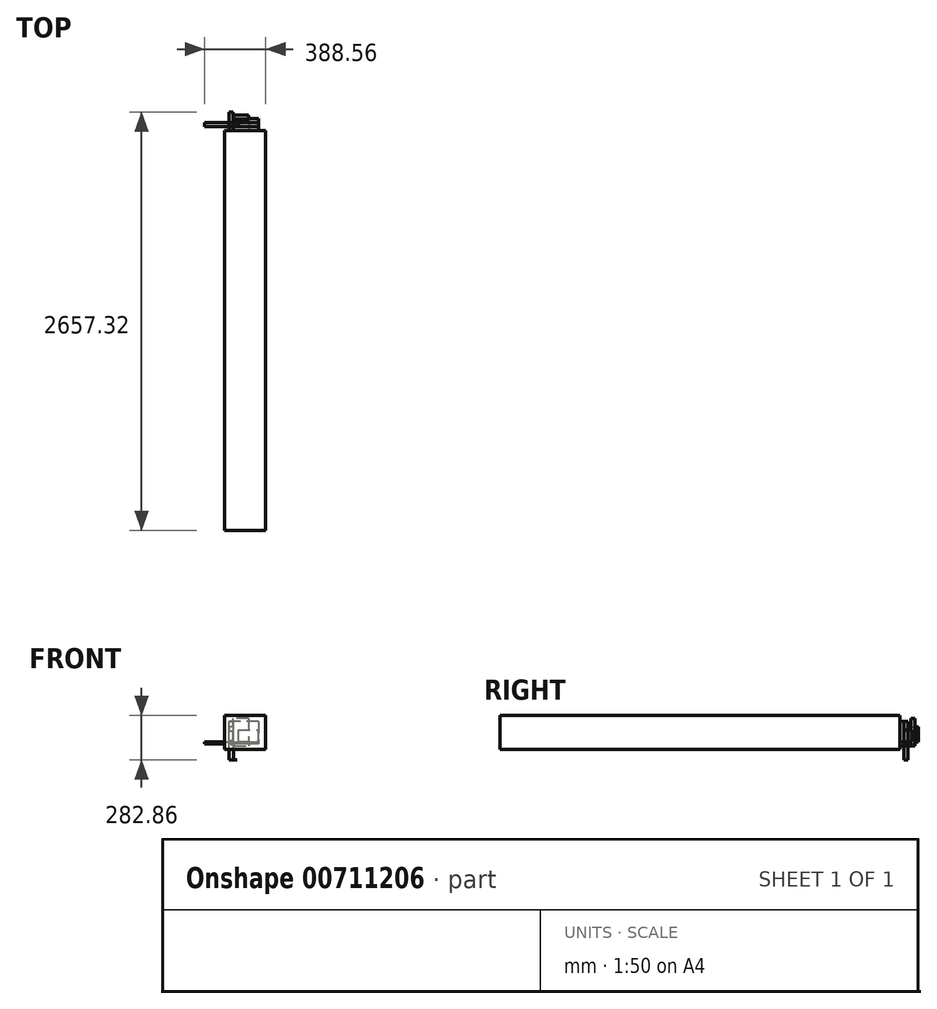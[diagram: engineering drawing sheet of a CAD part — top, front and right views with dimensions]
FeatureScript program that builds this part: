
annotation { "Feature Type Name" : "Feature", "Feature Type Description" : "" }
export const myFeature = defineFeature(function(context is Context, id is Id, definition is map)
    precondition{}
    {
        {
            var Q0;
            Q0=qCreatedBy(makeId("Front.planeOp"),FACE);
            var sketch = newSketch(context, id + "F0", { "sketchPlane" : qUnion([Q0])});
            skLineSegment(sketch, "E0.bottom", {"start": v(0, 0) * mm, "end": v(78.63, 0) * mm});
            skLineSegment(sketch, "E0.top", {"start": v(0, -50.24) * mm, "end": v(78.63, -50.24) * mm});
            skLineSegment(sketch, "E0.left", {"start": v(0, 0) * mm, "end": v(0, -50.24) * mm});
            skLineSegment(sketch, "E0.right", {"start": v(78.63, 0) * mm, "end": v(78.63, -50.24) * mm});
            skLineSegment(sketch, "E1.bottom", {"start": v(78.63, 0) * mm, "end": v(-83, 0) * mm});
            skLineSegment(sketch, "E1.top", {"start": v(78.63, 52.99) * mm, "end": v(-83, 52.99) * mm});
            skLineSegment(sketch, "E1.left", {"start": v(78.63, 0) * mm, "end": v(78.63, 52.99) * mm});
            skLineSegment(sketch, "E1.right", {"start": v(-83, 0) * mm, "end": v(-83, 52.99) * mm});
            skLineSegment(sketch, "E2.bottom", {"start": v(-83, 0) * mm, "end": v(0, 0) * mm});
            skLineSegment(sketch, "E2.top", {"start": v(-83, -50.24) * mm, "end": v(0, -50.24) * mm});
            skLineSegment(sketch, "E2.left", {"start": v(-83, 0) * mm, "end": v(-83, -50.24) * mm});
            skSolve(sketch);
        }
        {
            var Q0;
            Q0 = qSketchRegion(id + "F0", true);
            extrude(context, id + "F1", {"entities" : qUnion([Q0]), "depth" : 25.4 * mm, "offsetDistance" : 25.4 * mm});
        }
        {
            var Q0;
            Q0=makeQuery(id+"F1.opExtrude","SWEPT_FACE",FACE,{"disambiguationData":[OSD([sQuery(id+"F0.wireOp",EDGE,"E0.top"),sQuery(id+"F0.wireOp",EDGE,"E2.top")])]});
            var sketch = newSketch(context, id + "F2", { "sketchPlane" : qUnion([Q0])});
            skLineSegment(sketch, "E3.bottom", {"start": v(-56.4, 25.75) * mm, "end": v(78.63, 25.75) * mm});
            skLineSegment(sketch, "E3.top", {"start": v(-56.4, 0) * mm, "end": v(78.63, 0) * mm});
            skLineSegment(sketch, "E3.left", {"start": v(-56.4, 25.75) * mm, "end": v(-56.4, 0) * mm});
            skLineSegment(sketch, "E3.right", {"start": v(78.63, 25.75) * mm, "end": v(78.63, 0) * mm});
            skLineSegment(sketch, "E4.bottom", {"start": v(-56.4, 0) * mm, "end": v(-83, 0) * mm});
            skLineSegment(sketch, "E4.top", {"start": v(-56.4, 25.4) * mm, "end": v(-83, 25.4) * mm});
            skLineSegment(sketch, "E4.left", {"start": v(-56.4, 0) * mm, "end": v(-56.4, 25.4) * mm});
            skLineSegment(sketch, "E4.right", {"start": v(-83, 0) * mm, "end": v(-83, 25.4) * mm});
            skLineSegment(sketch, "E5.bottom", {"start": v(-56.4, 25.4) * mm, "end": v(77.16, 25.4) * mm});
            skLineSegment(sketch, "E5.top", {"start": v(-56.4, 25.4) * mm, "end": v(77.16, 25.4) * mm});
            skLineSegment(sketch, "E5.left", {"start": v(-56.4, 25.4) * mm, "end": v(-56.4, 25.4) * mm});
            skLineSegment(sketch, "E5.right", {"start": v(77.16, 25.4) * mm, "end": v(77.16, 25.4) * mm});
            skLineSegment(sketch, "E6.bottom", {"start": v(78.63, 0) * mm, "end": v(77.16, 0) * mm});
            skLineSegment(sketch, "E6.top", {"start": v(78.63, 25.4) * mm, "end": v(77.16, 25.4) * mm});
            skLineSegment(sketch, "E6.left", {"start": v(78.63, 0) * mm, "end": v(78.63, 25.4) * mm});
            skLineSegment(sketch, "E6.right", {"start": v(77.16, 0) * mm, "end": v(77.16, 25.4) * mm});
            skLineSegment(sketch, "E7.bottom", {"start": v(-56.4, 12.7) * mm, "end": v(-83, 12.7) * mm});
            skLineSegment(sketch, "E7.left", {"start": v(-56.4, 12.7) * mm, "end": v(-56.4, 0) * mm});
            skLineSegment(sketch, "E7.right", {"start": v(-83, 12.7) * mm, "end": v(-83, 0) * mm});
            skSolve(sketch);
        }
        {
            var Q0;
            Q0 = qSketchRegion(id + "F2", true);
            extrude(context, id + "F3", {"entities" : qUnion([Q0]), "operationType" : NewBodyOperationType.ADD, "depth" : 25.4 * mm, "offsetDistance" : 25.4 * mm});
        }
        {
            var Q0;
            Q0=makeQuery(id+"F3.boolean.opBoolean","MERGE",FACE,{"derivedFrom":[makeQuery(id+"F1.opExtrude","CAP_FACE",FACE,{"disambiguationData":[OSD([sQuery(id+"F0.wireOp",EDGE,"E0.top"),sQuery(id+"F0.wireOp",EDGE,"E0.right"),sQuery(id+"F0.wireOp",EDGE,"E1.top"),sQuery(id+"F0.wireOp",EDGE,"E1.left"),sQuery(id+"F0.wireOp",EDGE,"E1.right"),sQuery(id+"F0.wireOp",EDGE,"E2.top"),sQuery(id+"F0.wireOp",EDGE,"E2.left")])],"isStart":false}),makeQuery(id+"F3.opExtrude","SWEPT_FACE",FACE,{"disambiguationData":[OSD([sQuery(id+"F2.wireOp",EDGE,"E4.top")])]})]});
            var sketch = newSketch(context, id + "F4", { "sketchPlane" : qUnion([Q0])});
            skLineSegment(sketch, "E8.bottom", {"start": v(124.19, 91.37) * mm, "end": v(-137.15, 91.37) * mm});
            skLineSegment(sketch, "E8.top", {"start": v(124.19, -123.53) * mm, "end": v(-137.15, -123.53) * mm});
            skLineSegment(sketch, "E8.left", {"start": v(124.19, 91.37) * mm, "end": v(124.19, -123.53) * mm});
            skLineSegment(sketch, "E8.right", {"start": v(-137.15, 91.37) * mm, "end": v(-137.15, -123.53) * mm});
            skSolve(sketch);
        }
        {
            var Q0;
            Q0 = qSketchRegion(id + "F4", true);
            extrude(context, id + "F5", {"entities" : qUnion([Q0]), "operationType" : NewBodyOperationType.ADD, "depth" : 2540 * mm, "offsetDistance" : 25.4 * mm});
        }
        {
            var Q0;
            Q0=makeQuery(id+"F3.boolean.opBoolean","MERGE",FACE,{"derivedFrom":[makeQuery(id+"F1.opExtrude","SWEPT_FACE",FACE,{"disambiguationData":[OSD([sQuery(id+"F0.wireOp",EDGE,"E1.right"),sQuery(id+"F0.wireOp",EDGE,"E2.left")])]}),makeQuery(id+"F3.opExtrude","SWEPT_FACE",FACE,{"disambiguationData":[OSD([sQuery(id+"F2.wireOp",EDGE,"E4.right"),sQuery(id+"F2.wireOp",EDGE,"E7.right")])]})]});
            var sketch = newSketch(context, id + "F6", { "sketchPlane" : qUnion([Q0])});
            skLineSegment(sketch, "E9.bottom", {"start": v(0, -75.64) * mm, "end": v(-91.92, -75.64) * mm});
            skLineSegment(sketch, "E9.top", {"start": v(0, -7.44) * mm, "end": v(-91.92, -7.44) * mm});
            skLineSegment(sketch, "E9.left", {"start": v(0, -75.64) * mm, "end": v(0, -7.44) * mm});
            skLineSegment(sketch, "E9.right", {"start": v(-91.92, -75.64) * mm, "end": v(-91.92, -7.44) * mm});
            skSolve(sketch);
        }
        {
            var Q0;
            Q0 = qSketchRegion(id + "F6", true);
            extrude(context, id + "F7", {"entities" : qUnion([Q0]), "depth" : 25.4 * mm, "offsetDistance" : 25.4 * mm});
        }
        {
            var Q0;
            Q0=makeQuery(id+"F3.boolean.opBoolean","MERGE",FACE,{"derivedFrom":[makeQuery(id+"F1.opExtrude","SWEPT_FACE",FACE,{"disambiguationData":[OSD([sQuery(id+"F0.wireOp",EDGE,"E1.right"),sQuery(id+"F0.wireOp",EDGE,"E2.left")])]}),makeQuery(id+"F3.opExtrude","SWEPT_FACE",FACE,{"disambiguationData":[OSD([sQuery(id+"F2.wireOp",EDGE,"E4.right"),sQuery(id+"F2.wireOp",EDGE,"E7.right")])]})]});
            var sketch = newSketch(context, id + "F8", { "sketchPlane" : qUnion([Q0])});
            skLineSegment(sketch, "E10.bottom", {"start": v(0, -58.88) * mm, "end": v(18.18, -58.88) * mm});
            skLineSegment(sketch, "E10.top", {"start": v(0, -75.64) * mm, "end": v(18.18, -75.64) * mm});
            skLineSegment(sketch, "E10.left", {"start": v(0, -58.88) * mm, "end": v(0, -75.64) * mm});
            skLineSegment(sketch, "E10.right", {"start": v(18.18, -58.88) * mm, "end": v(18.18, -75.64) * mm});
            skLineSegment(sketch, "E11.bottom", {"start": v(18.18, -75.64) * mm, "end": v(25.4, -75.64) * mm});
            skLineSegment(sketch, "E11.top", {"start": v(18.18, 52.99) * mm, "end": v(25.4, 52.99) * mm});
            skLineSegment(sketch, "E11.left", {"start": v(18.18, -75.64) * mm, "end": v(18.18, 52.99) * mm});
            skLineSegment(sketch, "E11.right", {"start": v(25.4, -75.64) * mm, "end": v(25.4, 52.99) * mm});
            skLineSegment(sketch, "E12.bottom", {"start": v(18.18, 52.99) * mm, "end": v(0, 52.99) * mm});
            skLineSegment(sketch, "E12.top", {"start": v(18.18, -75.64) * mm, "end": v(0, -75.64) * mm});
            skLineSegment(sketch, "E12.left", {"start": v(18.18, 52.99) * mm, "end": v(18.18, -75.64) * mm});
            skLineSegment(sketch, "E12.right", {"start": v(0, 52.99) * mm, "end": v(0, -75.64) * mm});
            skLineSegment(sketch, "E13.bottom", {"start": v(25.4, -75.64) * mm, "end": v(25.4, -75.64) * mm});
            skLineSegment(sketch, "E13.top", {"start": v(25.4, 52.99) * mm, "end": v(25.4, 52.99) * mm});
            skSolve(sketch);
        }
        {
            var Q0;
            Q0 = qSketchRegion(id + "F8", true);
            extrude(context, id + "F9", {"entities" : qUnion([Q0]), "depth" : 25.4 * mm, "offsetDistance" : 25.4 * mm});
        }
        {
            var Q0;
            Q0=makeQuery(id+"F9.opExtrude","SWEPT_FACE",FACE,{"disambiguationData":[OSD([sQuery(id+"F8.wireOp",EDGE,"E12.right")])]});
            var sketch = newSketch(context, id + "F10", { "sketchPlane" : qUnion([Q0])});
            skLineSegment(sketch, "E14.bottom", {"start": v(58.99, -191.49) * mm, "end": v(78.82, -191.49) * mm});
            skLineSegment(sketch, "E14.top", {"start": v(58.99, -190.19) * mm, "end": v(78.82, -190.19) * mm});
            skLineSegment(sketch, "E14.left", {"start": v(58.99, -191.49) * mm, "end": v(58.99, -190.19) * mm});
            skLineSegment(sketch, "E14.right", {"start": v(78.82, -191.49) * mm, "end": v(78.82, -190.19) * mm});
            skLineSegment(sketch, "E15.bottom", {"start": v(78.82, -190.19) * mm, "end": v(108.4, -190.19) * mm});
            skLineSegment(sketch, "E15.top", {"start": v(78.82, 52.99) * mm, "end": v(108.4, 52.99) * mm});
            skLineSegment(sketch, "E15.left", {"start": v(78.82, -190.19) * mm, "end": v(78.82, 52.99) * mm});
            skLineSegment(sketch, "E15.right", {"start": v(108.4, -190.19) * mm, "end": v(108.4, 52.99) * mm});
            skSolve(sketch);
        }
        {
            var Q0;
            Q0 = qSketchRegion(id + "F10", true);
            extrude(context, id + "F11", {"entities" : qUnion([Q0]), "depth" : 25.4 * mm, "offsetDistance" : 25.4 * mm});
        }
        {
            var Q0;
            Q0=makeQuery(id+"F7.opExtrude","SWEPT_FACE",FACE,{"disambiguationData":[OSD([sQuery(id+"F6.wireOp",EDGE,"E9.top")])]});
            var sketch = newSketch(context, id + "F12", { "sketchPlane" : qUnion([Q0])});
            skLineSegment(sketch, "E16.bottom", {"start": v(-108.4, 91.92) * mm, "end": v(-83, 91.92) * mm});
            skLineSegment(sketch, "E16.top", {"start": v(-108.4, 91.92) * mm, "end": v(-83, 91.92) * mm});
            skLineSegment(sketch, "E16.left", {"start": v(-108.4, 91.92) * mm, "end": v(-108.4, 91.92) * mm});
            skLineSegment(sketch, "E16.right", {"start": v(-83, 91.92) * mm, "end": v(-83, 91.92) * mm});
            skLineSegment(sketch, "E17.bottom", {"start": v(-83, 91.92) * mm, "end": v(-108.4, 91.92) * mm});
            skLineSegment(sketch, "E17.top", {"start": v(-83, 20.87) * mm, "end": v(-108.4, 20.87) * mm});
            skLineSegment(sketch, "E17.left", {"start": v(-83, 91.92) * mm, "end": v(-83, 20.87) * mm});
            skLineSegment(sketch, "E17.right", {"start": v(-108.4, 91.92) * mm, "end": v(-108.4, 20.87) * mm});
            skSolve(sketch);
        }
        {
            var Q0;
            Q0 = qSketchRegion(id + "F12", true);
            extrude(context, id + "F13", {"entities" : qUnion([Q0]), "depth" : 25.4 * mm, "offsetDistance" : 25.4 * mm});
        }
        {
            var Q0;
            Q0=makeQuery(id+"F3.boolean.opBoolean","MERGE",FACE,{"derivedFrom":[makeQuery(id+"F1.opExtrude","CAP_FACE",FACE,{"disambiguationData":[OSD([sQuery(id+"F0.wireOp",EDGE,"E0.top"),sQuery(id+"F0.wireOp",EDGE,"E0.right"),sQuery(id+"F0.wireOp",EDGE,"E1.top"),sQuery(id+"F0.wireOp",EDGE,"E1.left"),sQuery(id+"F0.wireOp",EDGE,"E1.right"),sQuery(id+"F0.wireOp",EDGE,"E2.top"),sQuery(id+"F0.wireOp",EDGE,"E2.left")])],"isStart":true}),makeQuery(id+"F3.opExtrude","SWEPT_FACE",FACE,{"disambiguationData":[OSD([sQuery(id+"F2.wireOp",EDGE,"E3.top"),sQuery(id+"F2.wireOp",EDGE,"E6.bottom"),sQuery(id+"F2.wireOp",EDGE,"E4.bottom")])]})]});
            var sketch = newSketch(context, id + "F14", { "sketchPlane" : qUnion([Q0])});
            skLineSegment(sketch, "E18.bottom", {"start": v(78.47, -80.98) * mm, "end": v(101.83, -80.98) * mm});
            skLineSegment(sketch, "E18.top", {"start": v(78.47, -69.53) * mm, "end": v(101.83, -69.53) * mm});
            skLineSegment(sketch, "E18.left", {"start": v(78.47, -80.98) * mm, "end": v(78.47, -69.53) * mm});
            skLineSegment(sketch, "E18.right", {"start": v(101.83, -80.98) * mm, "end": v(101.83, -69.53) * mm});
            skLineSegment(sketch, "E19.bottom", {"start": v(78.47, -80.98) * mm, "end": v(100.27, -80.98) * mm});
            skLineSegment(sketch, "E19.top", {"start": v(78.47, -80.98) * mm, "end": v(100.27, -80.98) * mm});
            skLineSegment(sketch, "E19.left", {"start": v(78.47, -80.98) * mm, "end": v(78.47, -80.98) * mm});
            skLineSegment(sketch, "E19.right", {"start": v(100.27, -80.98) * mm, "end": v(100.27, -80.98) * mm});
            skLineSegment(sketch, "E20.bottom", {"start": v(100.27, -80.98) * mm, "end": v(78.47, -80.98) * mm});
            skLineSegment(sketch, "E20.top", {"start": v(100.27, -91.98) * mm, "end": v(78.47, -91.98) * mm});
            skLineSegment(sketch, "E20.left", {"start": v(100.27, -80.98) * mm, "end": v(100.27, -91.98) * mm});
            skLineSegment(sketch, "E20.right", {"start": v(78.47, -80.98) * mm, "end": v(78.47, -91.98) * mm});
            skSolve(sketch);
        }
        {
            var Q0;
            Q0 = qSketchRegion(id + "F14", true);
            extrude(context, id + "F15", {"entities" : qUnion([Q0]), "depth" : 25.4 * mm, "offsetDistance" : 25.4 * mm});
        }
        {
            var Q0;
            Q0=makeQuery(id+"F3.opExtrude","CAP_FACE",FACE,{"disambiguationData":[OSD([sQuery(id+"F2.wireOp",EDGE,"E3.bottom"),sQuery(id+"F2.wireOp",EDGE,"E3.top"),sQuery(id+"F2.wireOp",EDGE,"E3.left"),sQuery(id+"F2.wireOp",EDGE,"E3.right"),sQuery(id+"F2.wireOp",EDGE,"E4.top"),sQuery(id+"F2.wireOp",EDGE,"E4.right"),sQuery(id+"F2.wireOp",EDGE,"E6.bottom"),sQuery(id+"F2.wireOp",EDGE,"E6.left"),sQuery(id+"F2.wireOp",EDGE,"E4.bottom"),sQuery(id+"F2.wireOp",EDGE,"E7.right")])],"isStart":false});
            var sketch = newSketch(context, id + "F16", { "sketchPlane" : qUnion([Q0])});
            skLineSegment(sketch, "E21.bottom", {"start": v(-74.07, 25.4) * mm, "end": v(21.2, 25.4) * mm});
            skLineSegment(sketch, "E21.top", {"start": v(-74.07, -47.2) * mm, "end": v(21.2, -47.2) * mm});
            skLineSegment(sketch, "E21.left", {"start": v(-74.07, 25.4) * mm, "end": v(-74.07, -47.2) * mm});
            skLineSegment(sketch, "E21.right", {"start": v(21.2, 25.4) * mm, "end": v(21.2, -47.2) * mm});
            skSolve(sketch);
        }
        {
            var Q0;
            Q0 = qSketchRegion(id + "F16", true);
            extrude(context, id + "F17", {"entities" : qUnion([Q0]), "operationType" : NewBodyOperationType.ADD, "depth" : 25.4 * mm, "offsetDistance" : 25.4 * mm});
        }
        {
            var Q0;
            Q0=makeQuery(id+"F17.opExtrude","SWEPT_FACE",FACE,{"disambiguationData":[OSD([sQuery(id+"F16.wireOp",EDGE,"E21.top")])]});
            var sketch = newSketch(context, id + "F18", { "sketchPlane" : qUnion([Q0])});
            skLineSegment(sketch, "E22.bottom", {"start": v(74.07, -88.34) * mm, "end": v(-14.84, -88.34) * mm});
            skLineSegment(sketch, "E22.top", {"start": v(74.07, -101.04) * mm, "end": v(-14.84, -101.04) * mm});
            skLineSegment(sketch, "E22.left", {"start": v(74.07, -88.34) * mm, "end": v(74.07, -101.04) * mm});
            skLineSegment(sketch, "E22.right", {"start": v(-14.84, -88.34) * mm, "end": v(-14.84, -101.04) * mm});
            skLineSegment(sketch, "E23.bottom", {"start": v(-14.84, -88.34) * mm, "end": v(83.82, -88.34) * mm});
            skLineSegment(sketch, "E23.top", {"start": v(-14.84, 73.44) * mm, "end": v(83.82, 73.44) * mm});
            skLineSegment(sketch, "E23.left", {"start": v(-14.84, -88.34) * mm, "end": v(-14.84, 73.44) * mm});
            skLineSegment(sketch, "E23.right", {"start": v(83.82, -88.34) * mm, "end": v(83.82, 73.44) * mm});
            skSolve(sketch);
        }
        {
            var Q0;
            Q0 = qSketchRegion(id + "F18", true);
            extrude(context, id + "F19", {"entities" : qUnion([Q0]), "depth" : 25.4 * mm, "offsetDistance" : 25.4 * mm});
        }
        {
            var Q0;
            Q0=makeQuery(id+"F3.boolean.opBoolean","MERGE",FACE,{"derivedFrom":[makeQuery(id+"F1.opExtrude","CAP_FACE",FACE,{"disambiguationData":[OSD([sQuery(id+"F0.wireOp",EDGE,"E0.top"),sQuery(id+"F0.wireOp",EDGE,"E0.right"),sQuery(id+"F0.wireOp",EDGE,"E1.top"),sQuery(id+"F0.wireOp",EDGE,"E1.left"),sQuery(id+"F0.wireOp",EDGE,"E1.right"),sQuery(id+"F0.wireOp",EDGE,"E2.top"),sQuery(id+"F0.wireOp",EDGE,"E2.left")])],"isStart":true}),makeQuery(id+"F3.opExtrude","SWEPT_FACE",FACE,{"disambiguationData":[OSD([sQuery(id+"F2.wireOp",EDGE,"E3.top"),sQuery(id+"F2.wireOp",EDGE,"E6.bottom"),sQuery(id+"F2.wireOp",EDGE,"E4.bottom")])]})]});
            var sketch = newSketch(context, id + "F20", { "sketchPlane" : qUnion([Q0])});
            skLineSegment(sketch, "E24.bottom", {"start": v(-78.63, -75.64) * mm, "end": v(264.37, -75.64) * mm});
            skLineSegment(sketch, "E24.top", {"start": v(-78.63, -89.99) * mm, "end": v(264.37, -89.99) * mm});
            skLineSegment(sketch, "E24.left", {"start": v(-78.63, -75.64) * mm, "end": v(-78.63, -89.99) * mm});
            skLineSegment(sketch, "E24.right", {"start": v(264.37, -75.64) * mm, "end": v(264.37, -89.99) * mm});
            skSolve(sketch);
        }
        {
            var Q0;
            Q0 = qSketchRegion(id + "F20", true);
            extrude(context, id + "F21", {"entities" : qUnion([Q0]), "depth" : 25.4 * mm, "offsetDistance" : 25.4 * mm});
        }
        {
            var Q0;
            Q0=makeQuery(id+"F3.boolean.opBoolean","MERGE",FACE,{"derivedFrom":[makeQuery(id+"F1.opExtrude","CAP_FACE",FACE,{"disambiguationData":[OSD([sQuery(id+"F0.wireOp",EDGE,"E0.top"),sQuery(id+"F0.wireOp",EDGE,"E0.right"),sQuery(id+"F0.wireOp",EDGE,"E1.top"),sQuery(id+"F0.wireOp",EDGE,"E1.left"),sQuery(id+"F0.wireOp",EDGE,"E1.right"),sQuery(id+"F0.wireOp",EDGE,"E2.top"),sQuery(id+"F0.wireOp",EDGE,"E2.left")])],"isStart":true}),makeQuery(id+"F3.opExtrude","SWEPT_FACE",FACE,{"disambiguationData":[OSD([sQuery(id+"F2.wireOp",EDGE,"E3.top"),sQuery(id+"F2.wireOp",EDGE,"E6.bottom"),sQuery(id+"F2.wireOp",EDGE,"E4.bottom")])]})]});
            var sketch = newSketch(context, id + "F22", { "sketchPlane" : qUnion([Q0])});
            skLineSegment(sketch, "E25.bottom", {"start": v(49.35, -85.24) * mm, "end": v(-78.63, -85.24) * mm});
            skLineSegment(sketch, "E25.top", {"start": v(49.35, 0) * mm, "end": v(-78.63, 0) * mm});
            skLineSegment(sketch, "E25.left", {"start": v(49.35, -85.24) * mm, "end": v(49.35, 0) * mm});
            skLineSegment(sketch, "E25.right", {"start": v(-78.63, -85.24) * mm, "end": v(-78.63, 0) * mm});
            skSolve(sketch);
        }
        {
            var Q0;
            Q0 = qSketchRegion(id + "F22", true);
            extrude(context, id + "F23", {"entities" : qUnion([Q0]), "depth" : 25.4 * mm, "offsetDistance" : 25.4 * mm});
        }
        {
            var Q0;
            Q0=makeQuery(id+"F23.opExtrude","CAP_FACE",FACE,{"disambiguationData":[OSD([sQuery(id+"F22.wireOp",EDGE,"E25.bottom"),sQuery(id+"F22.wireOp",EDGE,"E25.top"),sQuery(id+"F22.wireOp",EDGE,"E25.left"),sQuery(id+"F22.wireOp",EDGE,"E25.right")])],"isStart":false});
            var sketch = newSketch(context, id + "F24", { "sketchPlane" : qUnion([Q0])});
            skLineSegment(sketch, "E26.bottom", {"start": v(49.35, -73.94) * mm, "end": v(-78.63, -73.94) * mm});
            skLineSegment(sketch, "E26.top", {"start": v(49.35, 0) * mm, "end": v(-78.63, 0) * mm});
            skLineSegment(sketch, "E26.left", {"start": v(49.35, -73.94) * mm, "end": v(49.35, 0) * mm});
            skLineSegment(sketch, "E26.right", {"start": v(-78.63, -73.94) * mm, "end": v(-78.63, 0) * mm});
            skSolve(sketch);
        }
        {
            var Q0;
            Q0 = qSketchRegion(id + "F24", true);
            extrude(context, id + "F25", {"entities" : qUnion([Q0]), "depth" : 25.4 * mm, "offsetDistance" : 25.4 * mm});
        }
    });
